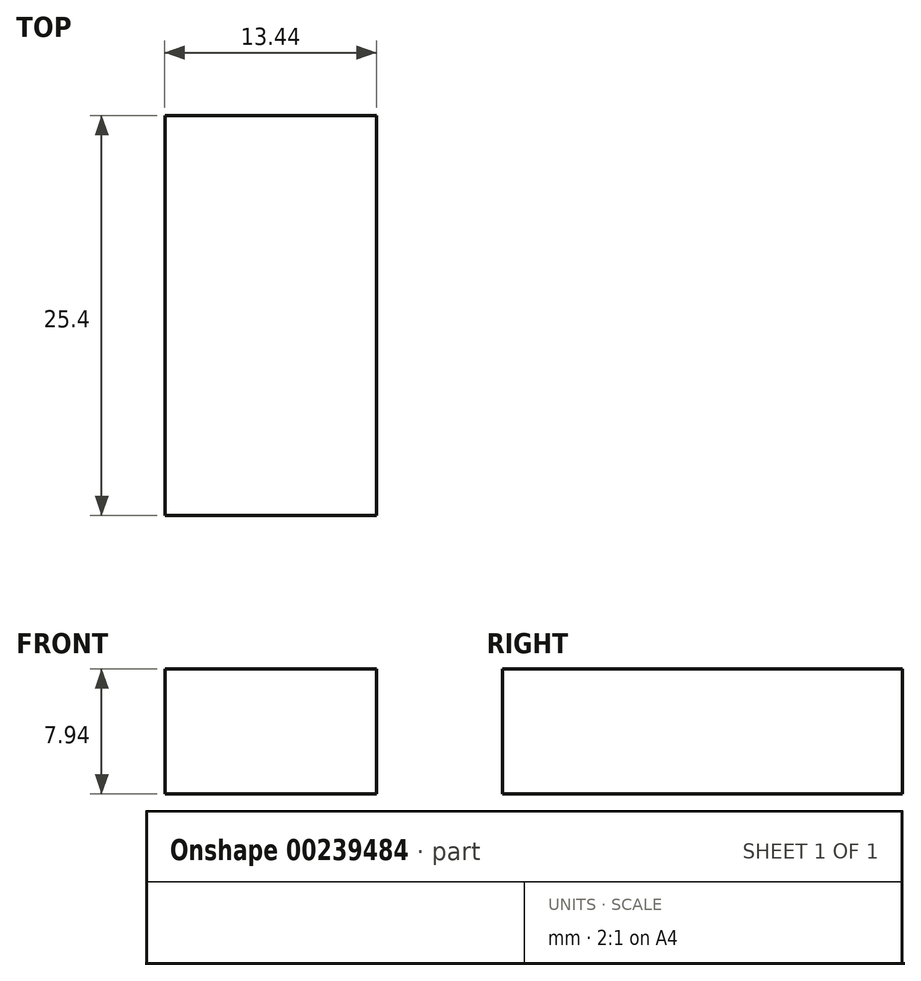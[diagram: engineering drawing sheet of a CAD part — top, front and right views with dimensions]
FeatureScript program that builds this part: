
annotation { "Feature Type Name" : "Feature", "Feature Type Description" : "" }
export const myFeature = defineFeature(function(context is Context, id is Id, definition is map)
    precondition{}
    {
        {
            var Q0;
            Q0=qCreatedBy(makeId("Front.planeOp"),FACE);
            var sketch = newSketch(context, id + "F0", { "sketchPlane" : qUnion([Q0])});
            skLineSegment(sketch, "E0.bottom", {"start": v(-6.72, 3.97) * mm, "end": v(6.72, 3.97) * mm});
            skLineSegment(sketch, "E0.top", {"start": v(-6.72, -3.97) * mm, "end": v(6.72, -3.97) * mm});
            skLineSegment(sketch, "E0.left", {"start": v(-6.72, 3.97) * mm, "end": v(-6.72, -3.97) * mm});
            skLineSegment(sketch, "E0.right", {"start": v(6.72, 3.97) * mm, "end": v(6.72, -3.97) * mm});
            skPoint(sketch, "E0.middle", {"position": v(0, 0) * mm});
            skSolve(sketch);
        }
        {
            var Q0;
            Q0 = qSketchRegion(id + "F0", true);
            extrude(context, id + "F1", {"entities" : qUnion([Q0]), "depth" : 25.4 * mm});
        }
    });
